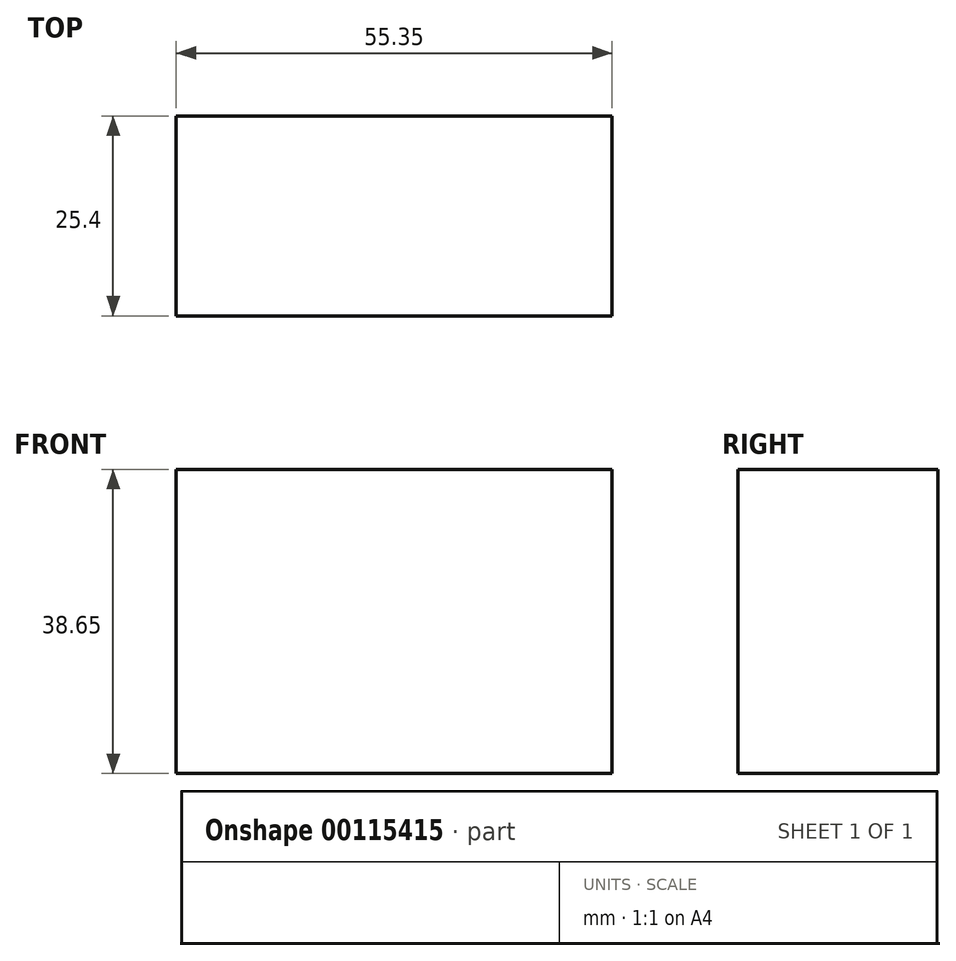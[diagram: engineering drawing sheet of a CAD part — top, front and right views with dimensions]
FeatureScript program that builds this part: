
annotation { "Feature Type Name" : "Feature", "Feature Type Description" : "" }
export const myFeature = defineFeature(function(context is Context, id is Id, definition is map)
    precondition{}
    {
        {
            var Q0;
            Q0=qCreatedBy(makeId("Front.planeOp"),FACE);
            var sketch = newSketch(context, id + "F0", { "sketchPlane" : qUnion([Q0])});
            skLineSegment(sketch, "E0", {"start": v(0, 0) * mm, "end": v(55.35, 0) * mm});
            skLineSegment(sketch, "E1", {"start": v(55.35, 0) * mm, "end": v(55.35, 38.65) * mm});
            skLineSegment(sketch, "E2", {"start": v(55.35, 38.65) * mm, "end": v(0, 38.65) * mm});
            skLineSegment(sketch, "E3", {"start": v(0, 38.65) * mm, "end": v(0, 0) * mm});
            skSolve(sketch);
        }
        {
            var Q0;
            Q0 = qSketchRegion(id + "F0", true);
            extrude(context, id + "F1", {"entities" : qUnion([Q0]), "endBound" : BoundingType.SYMMETRIC, "oppositeDirection" : true, "depth" : 25.4 * mm});
        }
    });
